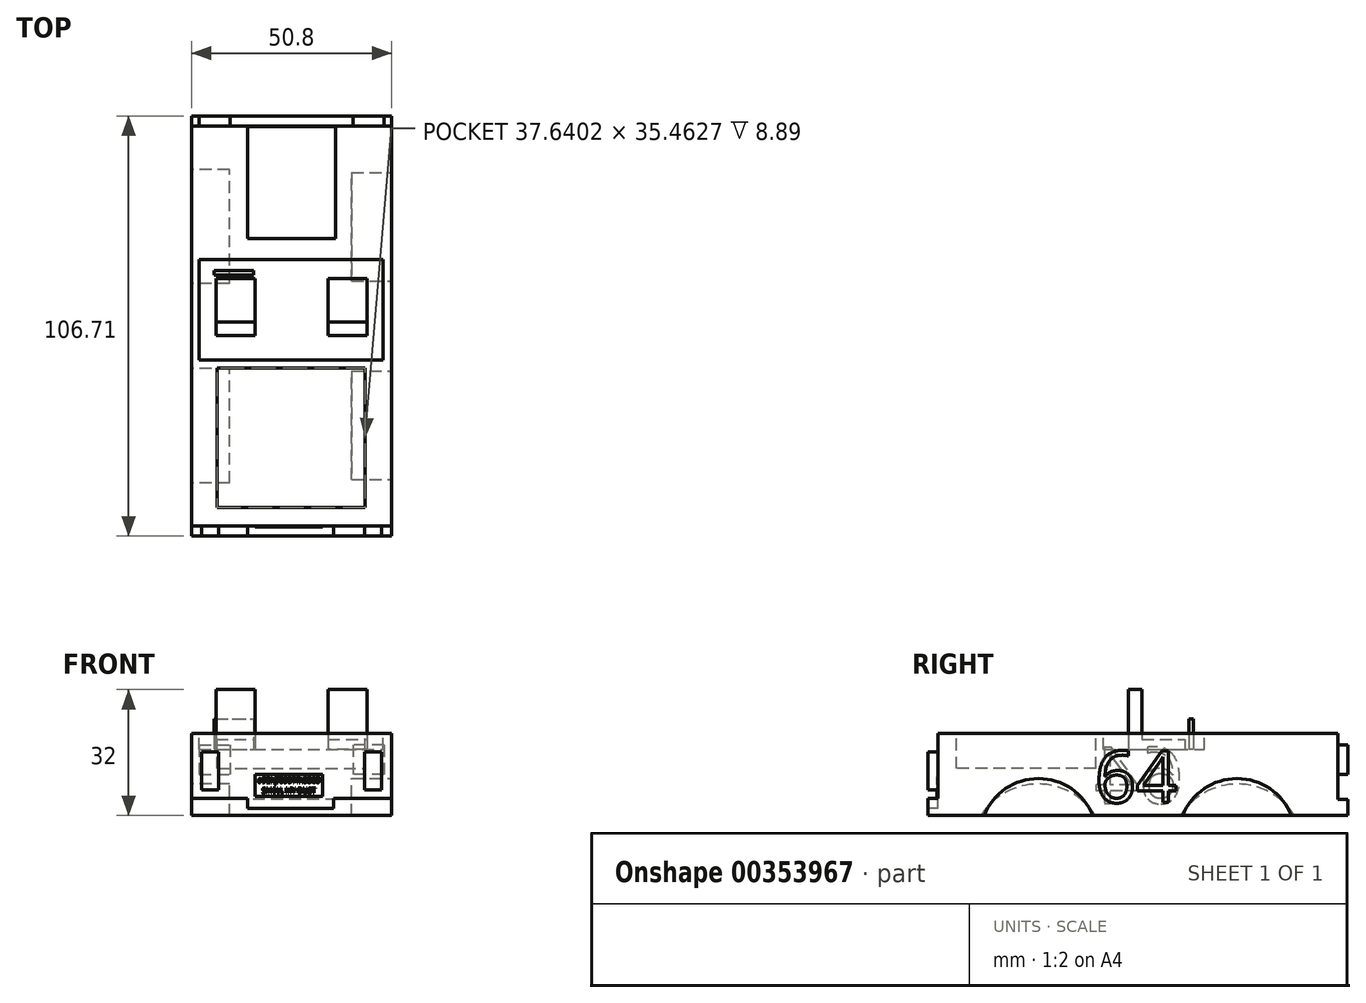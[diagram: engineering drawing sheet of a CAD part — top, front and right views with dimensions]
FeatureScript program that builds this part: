
annotation { "Feature Type Name" : "Feature", "Feature Type Description" : "" }
export const myFeature = defineFeature(function(context is Context, id is Id, definition is map)
    precondition{}
    {
        {
            var Q0;
            Q0=qCreatedBy(makeId("Top.planeOp"),FACE);
            var sketch = newSketch(context, id + "F0", { "sketchPlane" : qUnion([Q0])});
            skLineSegment(sketch, "E0.bottom", {"start": v(-25.4, -50.8) * mm, "end": v(25.4, -50.8) * mm});
            skLineSegment(sketch, "E0.top", {"start": v(-25.4, 50.8) * mm, "end": v(25.4, 50.8) * mm});
            skLineSegment(sketch, "E0.left", {"start": v(-25.4, -50.8) * mm, "end": v(-25.4, 50.8) * mm});
            skLineSegment(sketch, "E0.right", {"start": v(25.4, -50.8) * mm, "end": v(25.4, 50.8) * mm});
            skPoint(sketch, "E0.middle", {"position": v(0, 0) * mm});
            skSolve(sketch);
        }
        {
            var Q0;
            Q0 = qSketchRegion(id + "F0", true);
            extrude(context, id + "F1", {"entities" : qUnion([Q0]), "endBound" : BoundingType.SYMMETRIC, "depth" : 20.83 * mm});
        }
        {
            var Q0;
            Q0=makeQuery(id+"F1.opExtrude","SWEPT_FACE",FACE,{"disambiguationData":[OSD([sQuery(id+"F0.wireOp",EDGE,"E0.left")])]});
            var sketch = newSketch(context, id + "F2", { "sketchPlane" : qUnion([Q0])});
            skArc(sketch, "E1", {"start": v(-10.84, -10.41) * mm, "mid": v(-25.32, -2.43) * mm, "end": v(-39.8, -10.41) * mm});
            skLineSegment(sketch, "E2", {"start": v(-39.8, -10.41) * mm, "end": v(-10.84, -10.41) * mm});
            skArc(sketch, "E3.MirrorCS", {"start": v(10.84, -10.41) * mm, "mid": v(25.32, -2.43) * mm, "end": v(39.8, -10.41) * mm});
            skLineSegment(sketch, "E4.MirrorCS", {"start": v(39.8, -10.41) * mm, "end": v(10.84, -10.41) * mm});
            skSolve(sketch);
        }
        {
            var Q0;
            Q0 = qSketchRegion(id + "F2", true);
            extrude(context, id + "F3", {"entities" : qUnion([Q0]), "operationType" : NewBodyOperationType.REMOVE, "oppositeDirection" : true, "depth" : 9.65 * mm});
        }
        {
            var Q0;
            Q0=makeQuery(id+"F1.opExtrude","SWEPT_FACE",FACE,{"disambiguationData":[OSD([sQuery(id+"F0.wireOp",EDGE,"E0.right")])]});
            var sketch = newSketch(context, id + "F4", { "sketchPlane" : qUnion([Q0])});
            skArc(sketch, "E5", {"start": v(-11.43, -10.41) * mm, "mid": v(-25.22, -1.02) * mm, "end": v(-39.02, -10.41) * mm});
            skLineSegment(sketch, "E6", {"start": v(-39.02, -10.41) * mm, "end": v(-11.43, -10.41) * mm});
            skArc(sketch, "E7.MirrorCS", {"start": v(11.43, -10.41) * mm, "mid": v(25.22, -1.02) * mm, "end": v(39.02, -10.41) * mm});
            skLineSegment(sketch, "E8.MirrorCS", {"start": v(39.02, -10.41) * mm, "end": v(11.43, -10.41) * mm});
            skSolve(sketch);
        }
        {
            var Q0;
            Q0 = qSketchRegion(id + "F4", true);
            extrude(context, id + "F5", {"entities" : qUnion([Q0]), "operationType" : NewBodyOperationType.REMOVE, "oppositeDirection" : true, "depth" : 10.16 * mm});
        }
        {
            var Q0;
            Q0=makeQuery(id+"F1.opExtrude","CAP_FACE",FACE,{"disambiguationData":[OSD([sQuery(id+"F0.wireOp",EDGE,"E0.bottom"),sQuery(id+"F0.wireOp",EDGE,"E0.top"),sQuery(id+"F0.wireOp",EDGE,"E0.left"),sQuery(id+"F0.wireOp",EDGE,"E0.right")])],"isStart":false});
            var sketch = newSketch(context, id + "F6", { "sketchPlane" : qUnion([Q0])});
            skLineSegment(sketch, "E9.bottom", {"start": v(-18.92, -10.64) * mm, "end": v(18.72, -10.64) * mm});
            skLineSegment(sketch, "E9.top", {"start": v(-18.92, -46.1) * mm, "end": v(18.72, -46.1) * mm});
            skLineSegment(sketch, "E9.left", {"start": v(-18.92, -10.64) * mm, "end": v(-18.92, -46.1) * mm});
            skLineSegment(sketch, "E9.right", {"start": v(18.72, -10.64) * mm, "end": v(18.72, -46.1) * mm});
            skSolve(sketch);
        }
        {
            var Q0;
            Q0 = qSketchRegion(id + "F6", true);
            extrude(context, id + "F7", {"entities" : qUnion([Q0]), "operationType" : NewBodyOperationType.REMOVE, "oppositeDirection" : true, "depth" : 8.9 * mm});
        }
        {
            var Q0;
            Q0=makeQuery(id+"F1.opExtrude","CAP_FACE",FACE,{"disambiguationData":[OSD([sQuery(id+"F0.wireOp",EDGE,"E0.bottom"),sQuery(id+"F0.wireOp",EDGE,"E0.top"),sQuery(id+"F0.wireOp",EDGE,"E0.left"),sQuery(id+"F0.wireOp",EDGE,"E0.right")])],"isStart":false});
            var sketch = newSketch(context, id + "F8", { "sketchPlane" : qUnion([Q0])});
            skLineSegment(sketch, "E10.bottom", {"start": v(11.23, 22.27) * mm, "end": v(-11.23, 22.27) * mm});
            skLineSegment(sketch, "E10.top", {"start": v(11.23, 50.65) * mm, "end": v(-11.23, 50.65) * mm});
            skLineSegment(sketch, "E10.left", {"start": v(11.23, 22.27) * mm, "end": v(11.23, 50.65) * mm});
            skLineSegment(sketch, "E10.right", {"start": v(-11.23, 22.27) * mm, "end": v(-11.23, 50.65) * mm});
            skPoint(sketch, "E10.middle", {"position": v(0, 36.46) * mm});
            skSolve(sketch);
        }
        {
            var Q0;
            Q0 = qSketchRegion(id + "F8", true);
            extrude(context, id + "F9", {"entities" : qUnion([Q0]), "operationType" : NewBodyOperationType.ADD, "depth" : 0.03 * mm});
        }
        {
            var Q0;
            Q0=makeQuery(id+"F1.opExtrude","SWEPT_FACE",FACE,{"disambiguationData":[OSD([sQuery(id+"F0.wireOp",EDGE,"E0.top")])]});
            var sketch = newSketch(context, id + "F10", { "sketchPlane" : qUnion([Q0])});
            skLineSegment(sketch, "E11.bottom", {"start": v(-25.4, -10.41) * mm, "end": v(25.4, -10.41) * mm});
            skLineSegment(sketch, "E11.top", {"start": v(-25.4, -6.3) * mm, "end": v(25.4, -6.3) * mm});
            skLineSegment(sketch, "E11.left", {"start": v(-25.4, -10.41) * mm, "end": v(-25.4, -6.3) * mm});
            skLineSegment(sketch, "E11.right", {"start": v(25.4, -10.41) * mm, "end": v(25.4, -6.3) * mm});
            skLineSegment(sketch, "E12.bottom", {"start": v(-23.45, 7.49) * mm, "end": v(-15.57, 7.49) * mm});
            skLineSegment(sketch, "E12.top", {"start": v(-23.45, 0) * mm, "end": v(-15.57, 0) * mm});
            skLineSegment(sketch, "E12.left", {"start": v(-23.45, 7.49) * mm, "end": v(-23.45, 0) * mm});
            skLineSegment(sketch, "E12.right", {"start": v(-15.57, 7.49) * mm, "end": v(-15.57, 0) * mm});
            skLineSegment(sketch, "E13.MirrorCS", {"start": v(15.57, 7.49) * mm, "end": v(15.57, 0) * mm});
            skLineSegment(sketch, "E14.MirrorCS", {"start": v(23.45, 7.49) * mm, "end": v(15.57, 7.49) * mm});
            skLineSegment(sketch, "E15.MirrorCS", {"start": v(23.45, 7.49) * mm, "end": v(23.45, 0) * mm});
            skLineSegment(sketch, "E16.MirrorCS", {"start": v(23.45, 0) * mm, "end": v(15.57, 0) * mm});
            skSolve(sketch);
        }
        {
            var Q0;
            Q0 = qSketchRegion(id + "F10", true);
            extrude(context, id + "F11", {"entities" : qUnion([Q0]), "operationType" : NewBodyOperationType.ADD, "depth" : 2.54 * mm});
        }
        {
            var Q0;
            Q0=makeQuery(id+"F1.opExtrude","SWEPT_FACE",FACE,{"disambiguationData":[OSD([sQuery(id+"F0.wireOp",EDGE,"E0.bottom")])]});
            var sketch = newSketch(context, id + "F12", { "sketchPlane" : qUnion([Q0])});
            skLineSegment(sketch, "E17.bottom", {"start": v(-25.4, -10.41) * mm, "end": v(25.4, -10.41) * mm});
            skLineSegment(sketch, "E17.top", {"start": v(-25.4, -6.1) * mm, "end": v(25.4, -6.1) * mm});
            skLineSegment(sketch, "E17.left", {"start": v(-25.4, -10.41) * mm, "end": v(-25.4, -6.1) * mm});
            skLineSegment(sketch, "E17.right", {"start": v(25.4, -10.41) * mm, "end": v(25.4, -6.1) * mm});
            skLineSegment(sketch, "E18.bottom", {"start": v(-22.86, 5.72) * mm, "end": v(-18.52, 5.72) * mm});
            skLineSegment(sketch, "E18.top", {"start": v(-22.86, -3.94) * mm, "end": v(-18.52, -3.94) * mm});
            skLineSegment(sketch, "E18.left", {"start": v(-22.86, 5.72) * mm, "end": v(-22.86, -3.94) * mm});
            skLineSegment(sketch, "E18.right", {"start": v(-18.52, 5.72) * mm, "end": v(-18.52, -3.94) * mm});
            skLineSegment(sketch, "E19.MirrorCS", {"start": v(18.52, 5.72) * mm, "end": v(18.52, -3.94) * mm});
            skLineSegment(sketch, "E20.MirrorCS", {"start": v(22.86, 5.72) * mm, "end": v(18.52, 5.72) * mm});
            skLineSegment(sketch, "E21.MirrorCS", {"start": v(22.86, 5.72) * mm, "end": v(22.86, -3.94) * mm});
            skLineSegment(sketch, "E22.MirrorCS", {"start": v(22.86, -3.94) * mm, "end": v(18.52, -3.94) * mm});
            skSolve(sketch);
        }
        {
            var Q0;
            Q0 = qSketchRegion(id + "F12", true);
            extrude(context, id + "F13", {"entities" : qUnion([Q0]), "operationType" : NewBodyOperationType.ADD, "depth" : 2.54 * mm});
        }
        {
            var Q0;
            Q0 = qSketchRegion(id + "F10", true);
            extrude(context, id + "F14", {"entities" : qUnion([Q0]), "operationType" : NewBodyOperationType.ADD, "depth" : 2.57 * mm});
        }
        {
            var Q0;
            Q0=makeQuery(id+"F13.opExtrude","SWEPT_FACE",FACE,{"disambiguationData":[OSD([sQuery(id+"F12.wireOp",EDGE,"E17.top")])]});
            var sketch = newSketch(context, id + "F15", { "sketchPlane" : qUnion([Q0])});
            skLineSegment(sketch, "E23.bottom", {"start": v(-11.2, -50.8) * mm, "end": v(10.7, -50.8) * mm});
            skLineSegment(sketch, "E23.top", {"start": v(-11.2, -53.34) * mm, "end": v(10.7, -53.34) * mm});
            skLineSegment(sketch, "E23.left", {"start": v(-11.2, -50.8) * mm, "end": v(-11.2, -53.34) * mm});
            skLineSegment(sketch, "E23.right", {"start": v(10.7, -50.8) * mm, "end": v(10.7, -53.34) * mm});
            skSolve(sketch);
        }
        {
            var Q0;
            Q0 = qSketchRegion(id + "F15", true);
            extrude(context, id + "F16", {"entities" : qUnion([Q0]), "operationType" : NewBodyOperationType.REMOVE, "oppositeDirection" : true, "depth" : 2.54 * mm});
        }
        {
            var Q0;
            Q0=makeQuery(id+"F1.opExtrude","CAP_FACE",FACE,{"disambiguationData":[OSD([sQuery(id+"F0.wireOp",EDGE,"E0.bottom"),sQuery(id+"F0.wireOp",EDGE,"E0.top"),sQuery(id+"F0.wireOp",EDGE,"E0.left"),sQuery(id+"F0.wireOp",EDGE,"E0.right")])],"isStart":false});
            var sketch = newSketch(context, id + "F17", { "sketchPlane" : qUnion([Q0])});
            skLineSegment(sketch, "E24.bottom", {"start": v(-23.45, -8.67) * mm, "end": v(23.25, -8.67) * mm});
            skLineSegment(sketch, "E24.top", {"start": v(-23.45, 16.95) * mm, "end": v(23.25, 16.95) * mm});
            skLineSegment(sketch, "E24.left", {"start": v(-23.45, -8.67) * mm, "end": v(-23.45, 16.95) * mm});
            skLineSegment(sketch, "E24.right", {"start": v(23.25, -8.67) * mm, "end": v(23.25, 16.95) * mm});
            skSolve(sketch);
        }
        {
            var Q0;
            Q0 = qSketchRegion(id + "F17", true);
            extrude(context, id + "F18", {"entities" : qUnion([Q0]), "operationType" : NewBodyOperationType.REMOVE, "oppositeDirection" : true, "depth" : 4.06 * mm});
        }
        {
            var Q0;
            Q0=makeQuery(id+"F18.boolean.opBoolean","COPY",FACE,{"derivedFrom":makeQuery(id+"F18.opExtrude","CAP_FACE",FACE,{"disambiguationData":[OSD([sQuery(id+"F17.wireOp",EDGE,"E24.bottom"),sQuery(id+"F17.wireOp",EDGE,"E24.top"),sQuery(id+"F17.wireOp",EDGE,"E24.left"),sQuery(id+"F17.wireOp",EDGE,"E24.right")])],"isStart":false})});
            var sketch = newSketch(context, id + "F19", { "sketchPlane" : qUnion([Q0])});
            skLineSegment(sketch, "E25.bottom", {"start": v(19.12, -2.36) * mm, "end": v(9.26, -2.36) * mm});
            skLineSegment(sketch, "E25.top", {"start": v(19.12, 12.02) * mm, "end": v(9.26, 12.02) * mm});
            skLineSegment(sketch, "E25.left", {"start": v(19.12, -2.36) * mm, "end": v(19.12, 12.02) * mm});
            skLineSegment(sketch, "E25.right", {"start": v(9.26, -2.36) * mm, "end": v(9.26, 12.02) * mm});
            skLineSegment(sketch, "E26.MirrorCS", {"start": v(-19.12, -2.36) * mm, "end": v(-9.26, -2.36) * mm});
            skLineSegment(sketch, "E27.MirrorCS", {"start": v(-9.26, -2.36) * mm, "end": v(-9.26, 12.02) * mm});
            skLineSegment(sketch, "E28.MirrorCS", {"start": v(-19.12, 12.02) * mm, "end": v(-9.26, 12.02) * mm});
            skLineSegment(sketch, "E29.MirrorCS", {"start": v(-19.12, -2.36) * mm, "end": v(-19.12, 12.02) * mm});
            skSolve(sketch);
        }
        {
            var Q0;
            Q0 = qSketchRegion(id + "F19", true);
            extrude(context, id + "F20", {"entities" : qUnion([Q0]), "operationType" : NewBodyOperationType.ADD, "depth" : 2.54 * mm});
        }
        {
            var Q0;
            Q0=makeQuery(id+"F18.boolean.opBoolean","COPY",FACE,{"derivedFrom":makeQuery(id+"F18.opExtrude","CAP_FACE",FACE,{"disambiguationData":[OSD([sQuery(id+"F17.wireOp",EDGE,"E24.bottom"),sQuery(id+"F17.wireOp",EDGE,"E24.top"),sQuery(id+"F17.wireOp",EDGE,"E24.left"),sQuery(id+"F17.wireOp",EDGE,"E24.right")])],"isStart":false})});
            var sketch = newSketch(context, id + "F21", { "sketchPlane" : qUnion([Q0])});
            skLineSegment(sketch, "E30.bottom", {"start": v(19.12, -2.36) * mm, "end": v(9.26, -2.36) * mm});
            skLineSegment(sketch, "E30.top", {"start": v(19.12, 1.05) * mm, "end": v(9.26, 1.05) * mm});
            skLineSegment(sketch, "E30.left", {"start": v(19.12, -2.36) * mm, "end": v(19.12, 1.05) * mm});
            skLineSegment(sketch, "E30.right", {"start": v(9.26, -2.36) * mm, "end": v(9.26, 1.05) * mm});
            skLineSegment(sketch, "E31.MirrorCS", {"start": v(-19.12, -2.36) * mm, "end": v(-9.26, -2.36) * mm});
            skLineSegment(sketch, "E32.MirrorCS", {"start": v(-9.26, -2.36) * mm, "end": v(-9.26, 1.05) * mm});
            skLineSegment(sketch, "E33.MirrorCS", {"start": v(-19.12, 1.05) * mm, "end": v(-9.26, 1.05) * mm});
            skLineSegment(sketch, "E34.MirrorCS", {"start": v(-19.12, -2.36) * mm, "end": v(-19.12, 1.05) * mm});
            skSolve(sketch);
        }
        {
            var Q0;
            Q0 = qSketchRegion(id + "F21", true);
            extrude(context, id + "F22", {"entities" : qUnion([Q0]), "operationType" : NewBodyOperationType.ADD, "depth" : 15.24 * mm});
        }
        {
            var Q0;
            Q0=makeQuery(id+"F18.boolean.opBoolean","COPY",FACE,{"derivedFrom":makeQuery(id+"F18.opExtrude","CAP_FACE",FACE,{"disambiguationData":[OSD([sQuery(id+"F17.wireOp",EDGE,"E24.bottom"),sQuery(id+"F17.wireOp",EDGE,"E24.top"),sQuery(id+"F17.wireOp",EDGE,"E24.left"),sQuery(id+"F17.wireOp",EDGE,"E24.right")])],"isStart":false})});
            var sketch = newSketch(context, id + "F23", { "sketchPlane" : qUnion([Q0])});
            skLineSegment(sketch, "E35.bottom", {"start": v(-19.73, 14.1) * mm, "end": v(-9.62, 14.1) * mm});
            skLineSegment(sketch, "E35.top", {"start": v(-19.73, 12.94) * mm, "end": v(-9.62, 12.94) * mm});
            skLineSegment(sketch, "E35.left", {"start": v(-19.73, 14.1) * mm, "end": v(-19.73, 12.94) * mm});
            skLineSegment(sketch, "E35.right", {"start": v(-9.62, 14.1) * mm, "end": v(-9.62, 12.94) * mm});
            skSolve(sketch);
        }
        {
            var Q0;
            Q0 = qSketchRegion(id + "F23", true);
            extrude(context, id + "F24", {"entities" : qUnion([Q0]), "operationType" : NewBodyOperationType.ADD, "depth" : 7.75 * mm});
        }
        {
            var Q0;
            {var subQ0=sQuery(id+"F10.wireOp",EDGE,"E11.right");Q0=makeQuery(id+"F14.boolean.opBoolean","MERGE",FACE,{"derivedFrom":[makeQuery(id+"F13.boolean.opBoolean","MERGE",FACE,{"derivedFrom":[makeQuery(id+"F11.boolean.opBoolean","MERGE",FACE,{"derivedFrom":[makeQuery(id+"F1.opExtrude","SWEPT_FACE",FACE,{"disambiguationData":[OSD([sQuery(id+"F0.wireOp",EDGE,"E0.left")])]}),makeQuery(id+"F11.opExtrude","SWEPT_FACE",FACE,{"disambiguationData":[OSD([subQ0])]})]}),makeQuery(id+"F13.opExtrude","SWEPT_FACE",FACE,{"disambiguationData":[OSD([sQuery(id+"F12.wireOp",EDGE,"E17.left")])]})]}),makeQuery(id+"F14.opExtrude","SWEPT_FACE",FACE,{"disambiguationData":[OSD([subQ0])]})]});}
            var sketch = newSketch(context, id + "F25", { "sketchPlane" : qUnion([Q0])});
            skText(sketch, "E36", { "text": "64\n", "fontName": "OpenSans-Regular.ttf"});
            const initialGuessF25  = {"E36": [-0.01173, -0.0073, 1, 0, 0.01429]};
            skSetInitialGuess(sketch, initialGuessF25);
            skSolve(sketch);
        }
        {
            var Q0;
            Q0 = qSketchRegion(id + "F25", true);
            extrude(context, id + "F26", {"entities" : qUnion([Q0]), "operationType" : NewBodyOperationType.ADD, "depth" : 0 * mm});
        }
        {
            var Q0;
            {var subQ0=sQuery(id+"F10.wireOp",EDGE,"E11.left");Q0=makeQuery(id+"F14.boolean.opBoolean","MERGE",FACE,{"derivedFrom":[makeQuery(id+"F13.boolean.opBoolean","MERGE",FACE,{"derivedFrom":[makeQuery(id+"F11.boolean.opBoolean","MERGE",FACE,{"derivedFrom":[makeQuery(id+"F1.opExtrude","SWEPT_FACE",FACE,{"disambiguationData":[OSD([sQuery(id+"F0.wireOp",EDGE,"E0.right")])]}),makeQuery(id+"F11.opExtrude","SWEPT_FACE",FACE,{"disambiguationData":[OSD([subQ0])]})]}),makeQuery(id+"F13.opExtrude","SWEPT_FACE",FACE,{"disambiguationData":[OSD([sQuery(id+"F12.wireOp",EDGE,"E17.right")])]})]}),makeQuery(id+"F14.opExtrude","SWEPT_FACE",FACE,{"disambiguationData":[OSD([subQ0])]})]});}
            var sketch = newSketch(context, id + "F27", { "sketchPlane" : qUnion([Q0])});
            skText(sketch, "E37", { "text": "64\n", "fontName": "OpenSans-Regular.ttf"});
            const initialGuessF27  = {"E37": [-0.0109, -0.00713, 1, 0, 0.0132]};
            skSetInitialGuess(sketch, initialGuessF27);
            skSolve(sketch);
        }
        {
            var Q0;
            Q0 = qSketchRegion(id + "F27", true);
            extrude(context, id + "F28", {"entities" : qUnion([Q0]), "operationType" : NewBodyOperationType.ADD, "depth" : 0 * mm});
        }
        {
            var Q0;
            Q0=makeQuery(id+"F16.boolean.opBoolean","MERGE",FACE,{"derivedFrom":[makeQuery(id+"F1.opExtrude","SWEPT_FACE",FACE,{"disambiguationData":[OSD([sQuery(id+"F0.wireOp",EDGE,"E0.bottom")])]}),makeQuery(id+"F16.opExtrude","SWEPT_FACE",FACE,{"disambiguationData":[OSD([sQuery(id+"F15.wireOp",EDGE,"E23.bottom")])]})]});
            var sketch = newSketch(context, id + "F29", { "sketchPlane" : qUnion([Q0])});
            skLineSegment(sketch, "E38.bottom", {"start": v(-9.22, 0) * mm, "end": v(7.92, 0) * mm});
            skLineSegment(sketch, "E38.top", {"start": v(-9.22, -5.59) * mm, "end": v(7.92, -5.59) * mm});
            skLineSegment(sketch, "E38.left", {"start": v(-9.22, 0) * mm, "end": v(-9.22, -5.59) * mm});
            skLineSegment(sketch, "E38.right", {"start": v(7.92, 0) * mm, "end": v(7.92, -5.59) * mm});
            skSolve(sketch);
        }
        {
            var Q0;
            Q0 = qSketchRegion(id + "F29", true);
            extrude(context, id + "F30", {"entities" : qUnion([Q0]), "operationType" : NewBodyOperationType.ADD, "depth" : 0.25 * mm});
        }
        {
            var Q0;
            Q0=makeQuery(id+"F30.opExtrude","CAP_FACE",FACE,{"disambiguationData":[OSD([sQuery(id+"F29.wireOp",EDGE,"E38.bottom"),sQuery(id+"F29.wireOp",EDGE,"E38.top"),sQuery(id+"F29.wireOp",EDGE,"E38.left"),sQuery(id+"F29.wireOp",EDGE,"E38.right")])],"isStart":false});
            var sketch = newSketch(context, id + "F31", { "sketchPlane" : qUnion([Q0])});
            skText(sketch, "E39", { "text": "a92hjf8937fh3363", "fontName": "OpenSans-Regular.ttf"});
            skText(sketch, "E40", { "text": "SMELL MY DUST\n", "fontName": "OpenSans-Regular.ttf"});
            const initialGuessF31  = {"E39": [-0.00857, -0.00207, 1, 0, 0.00135], "E40": [-0.0075, -0.00473, 1, 0, 0.00129]};
            skSetInitialGuess(sketch, initialGuessF31);
            skSolve(sketch);
        }
        {
            var Q0;
            Q0 = qSketchRegion(id + "F31", true);
            extrude(context, id + "F32", {"entities" : qUnion([Q0]), "operationType" : NewBodyOperationType.ADD, "depth" : 0 * mm});
        }
    });
